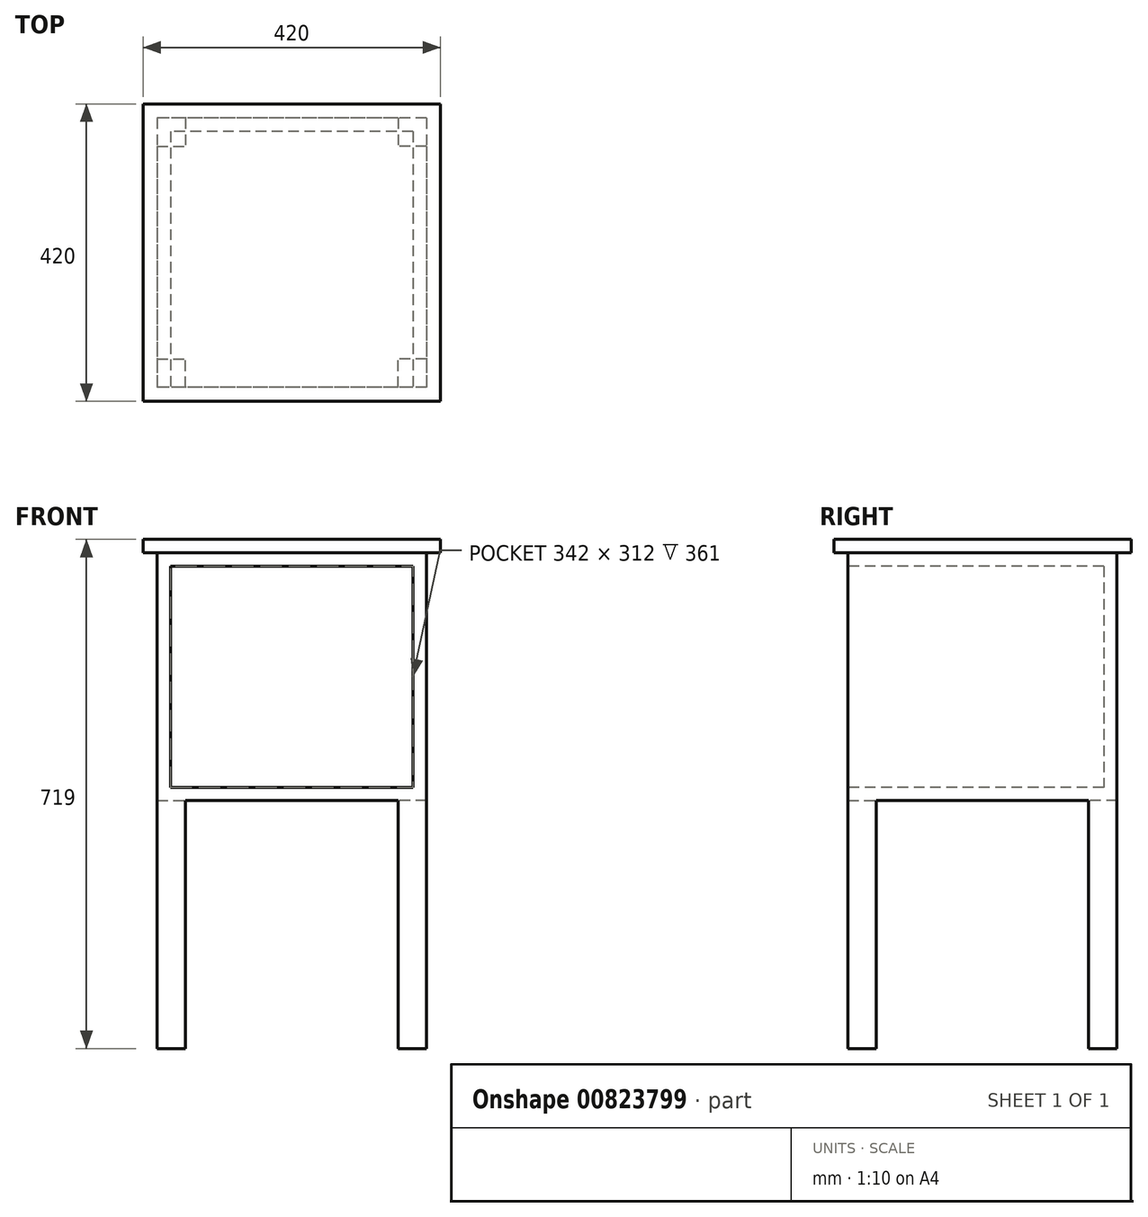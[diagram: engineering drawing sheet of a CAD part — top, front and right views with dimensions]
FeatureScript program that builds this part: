
annotation { "Feature Type Name" : "Feature", "Feature Type Description" : "" }
export const myFeature = defineFeature(function(context is Context, id is Id, definition is map)
    precondition{}
    {
        {
            var Q0;
            Q0=qCreatedBy(makeId("Top.planeOp"),FACE);
            var sketch = newSketch(context, id + "F0", { "sketchPlane" : qUnion([Q0])});
            skLineSegment(sketch, "E0.bottom", {"start": v(190, 190) * mm, "end": v(-190, 190) * mm});
            skLineSegment(sketch, "E0.top", {"start": v(190, -190) * mm, "end": v(-190, -190) * mm});
            skLineSegment(sketch, "E0.left", {"start": v(190, 190) * mm, "end": v(190, -190) * mm});
            skLineSegment(sketch, "E0.right", {"start": v(-190, 190) * mm, "end": v(-190, -190) * mm});
            skPoint(sketch, "E0.middle", {"position": v(0, 0) * mm});
            skSolve(sketch);
        }
        {
            var Q0;
            Q0 = qSketchRegion(id + "F0", true);
            extrude(context, id + "F1", {"entities" : qUnion([Q0]), "depth" : 350 * mm, "offsetDistance" : 25 * mm});
        }
        {
            var Q0;
            Q0=makeQuery(id+"F1.opExtrude","SWEPT_FACE",FACE,{"disambiguationData":[OSD([sQuery(id+"F0.wireOp",EDGE,"E0.top")])]});
            var sketch = newSketch(context, id + "F2", { "sketchPlane" : qUnion([Q0])});
            skLineSegment(sketch, "E1.bottom", {"start": v(171, 19) * mm, "end": v(-171, 19) * mm});
            skLineSegment(sketch, "E1.top", {"start": v(171, 331) * mm, "end": v(-171, 331) * mm});
            skLineSegment(sketch, "E1.left", {"start": v(171, 19) * mm, "end": v(171, 331) * mm});
            skLineSegment(sketch, "E1.right", {"start": v(-171, 19) * mm, "end": v(-171, 331) * mm});
            skPoint(sketch, "E1.middle", {"position": v(0, 175) * mm});
            skPoint(sketch, "E1.middle.positionSnap0", {"position": v(-190, 175) * mm});
            skPoint(sketch, "E1.centerSnap0", {"position": v(-190, 175) * mm});
            skSolve(sketch);
        }
        {
            var Q0;
            Q0=makeQuery(id+"F2.imprint","IMPRINT",FACE,{"disambiguationData":[TD([[makeQuery(id+"F2.imprint","IMPRINT",EDGE,{"derivedFrom":sQuery(id+"F2.wireOp",EDGE,"E1.bottom")}),-1.0]])]});
            extrude(context, id + "F3", {"entities" : qUnion([Q0]), "operationType" : NewBodyOperationType.ADD, "oppositeDirection" : true, "depth" : 361 * mm, "offsetDistance" : 25 * mm});
        }
        {
            var Q0;
            Q0=makeQuery(id+"F1.opExtrude","SWEPT_FACE",FACE,{"disambiguationData":[OSD([sQuery(id+"F0.wireOp",EDGE,"E0.top")])]});
            var sketch = newSketch(context, id + "F4", { "sketchPlane" : qUnion([Q0])});
            skLineSegment(sketch, "E2.bottom", {"start": v(171, 331) * mm, "end": v(-171, 331) * mm});
            skLineSegment(sketch, "E2.top", {"start": v(171, 19) * mm, "end": v(-171, 19) * mm});
            skLineSegment(sketch, "E2.left", {"start": v(171, 331) * mm, "end": v(171, 19) * mm});
            skLineSegment(sketch, "E2.right", {"start": v(-171, 331) * mm, "end": v(-171, 19) * mm});
            skPoint(sketch, "E2.middle", {"position": v(0, 175) * mm});
            skPoint(sketch, "E2.middle.positionSnap0", {"position": v(-190, 175) * mm});
            skPoint(sketch, "E2.centerSnap0", {"position": v(-190, 175) * mm});
            skSolve(sketch);
        }
        {
            var Q0;
            Q0=makeQuery(id+"F4.imprint","IMPRINT",FACE,{"disambiguationData":[TD([[makeQuery(id+"F4.imprint","IMPRINT",EDGE,{"derivedFrom":sQuery(id+"F4.wireOp",EDGE,"E2.bottom")}),1.0]])]});
            extrude(context, id + "F5", {"entities" : qUnion([Q0]), "operationType" : NewBodyOperationType.REMOVE, "oppositeDirection" : true, "depth" : 361 * mm, "offsetDistance" : 25 * mm});
        }
        {
            var Q0;
            Q0=makeQuery(id+"F1.opExtrude","CAP_FACE",FACE,{"disambiguationData":[OSD([sQuery(id+"F0.wireOp",EDGE,"E0.bottom"),sQuery(id+"F0.wireOp",EDGE,"E0.top"),sQuery(id+"F0.wireOp",EDGE,"E0.left"),sQuery(id+"F0.wireOp",EDGE,"E0.right")])],"isStart":true});
            var sketch = newSketch(context, id + "F6", { "sketchPlane" : qUnion([Q0])});
            skLineSegment(sketch, "E3.bottom", {"start": v(-190, 190) * mm, "end": v(-150, 190) * mm});
            skLineSegment(sketch, "E3.top", {"start": v(-190, 150) * mm, "end": v(-150, 150) * mm});
            skLineSegment(sketch, "E3.left", {"start": v(-190, 190) * mm, "end": v(-190, 150) * mm});
            skLineSegment(sketch, "E3.right", {"start": v(-150, 190) * mm, "end": v(-150, 150) * mm});
            skSolve(sketch);
        }
        {
            var Q0;
            Q0=makeQuery(id+"F6.imprint","IMPRINT",FACE,{"disambiguationData":[TD([[makeQuery(id+"F6.imprint","IMPRINT",EDGE,{"derivedFrom":sQuery(id+"F6.wireOp",EDGE,"E3.bottom")}),1.0]])]});
            extrude(context, id + "F7", {"entities" : qUnion([Q0]), "operationType" : NewBodyOperationType.ADD, "depth" : 150 * mm, "offsetDistance" : 25 * mm});
        }
        {
            var Q0;
            Q0=makeQuery(id+"F1.opExtrude","CAP_FACE",FACE,{"disambiguationData":[OSD([sQuery(id+"F0.wireOp",EDGE,"E0.bottom"),sQuery(id+"F0.wireOp",EDGE,"E0.top"),sQuery(id+"F0.wireOp",EDGE,"E0.left"),sQuery(id+"F0.wireOp",EDGE,"E0.right")])],"isStart":true});
            var sketch = newSketch(context, id + "F8", { "sketchPlane" : qUnion([Q0])});
            skLineSegment(sketch, "E4.bottom", {"start": v(190, 190) * mm, "end": v(150, 190) * mm});
            skLineSegment(sketch, "E4.top", {"start": v(190, 150) * mm, "end": v(150, 150) * mm});
            skLineSegment(sketch, "E4.left", {"start": v(190, 190) * mm, "end": v(190, 150) * mm});
            skLineSegment(sketch, "E4.right", {"start": v(150, 190) * mm, "end": v(150, 150) * mm});
            skSolve(sketch);
        }
        {
            var Q0;
            Q0=makeQuery(id+"F8.imprint","IMPRINT",FACE,{"disambiguationData":[TD([[makeQuery(id+"F8.imprint","IMPRINT",EDGE,{"derivedFrom":sQuery(id+"F8.wireOp",EDGE,"E4.bottom")}),1.0]])]});
            extrude(context, id + "F9", {"entities" : qUnion([Q0]), "operationType" : NewBodyOperationType.ADD, "depth" : 150 * mm, "offsetDistance" : 25 * mm});
        }
        {
            var Q0;
            Q0=makeQuery(id+"F1.opExtrude","CAP_FACE",FACE,{"disambiguationData":[OSD([sQuery(id+"F0.wireOp",EDGE,"E0.bottom"),sQuery(id+"F0.wireOp",EDGE,"E0.top"),sQuery(id+"F0.wireOp",EDGE,"E0.left"),sQuery(id+"F0.wireOp",EDGE,"E0.right")])],"isStart":true});
            var sketch = newSketch(context, id + "F10", { "sketchPlane" : qUnion([Q0])});
            skLineSegment(sketch, "E5.bottom", {"start": v(-190, -190) * mm, "end": v(-150, -190) * mm});
            skLineSegment(sketch, "E5.top", {"start": v(-190, -150) * mm, "end": v(-150, -150) * mm});
            skLineSegment(sketch, "E5.left", {"start": v(-190, -190) * mm, "end": v(-190, -150) * mm});
            skLineSegment(sketch, "E5.right", {"start": v(-150, -190) * mm, "end": v(-150, -150) * mm});
            skLineSegment(sketch, "E6.bottom", {"start": v(190, -190) * mm, "end": v(150, -190) * mm});
            skLineSegment(sketch, "E6.top", {"start": v(190, -150) * mm, "end": v(150, -150) * mm});
            skLineSegment(sketch, "E6.left", {"start": v(190, -190) * mm, "end": v(190, -150) * mm});
            skLineSegment(sketch, "E6.right", {"start": v(150, -190) * mm, "end": v(150, -150) * mm});
            skSolve(sketch);
        }
        {
            var Q0;
            Q0=makeQuery(id+"F10.imprint","IMPRINT",FACE,{"disambiguationData":[TD([[makeQuery(id+"F10.imprint","IMPRINT",EDGE,{"derivedFrom":sQuery(id+"F10.wireOp",EDGE,"E5.bottom")}),-1.0]])]});
            extrude(context, id + "F11", {"entities" : qUnion([Q0]), "operationType" : NewBodyOperationType.ADD, "depth" : 150 * mm, "offsetDistance" : 25 * mm});
        }
        {
            var Q0;
            Q0=makeQuery(id+"F1.opExtrude","CAP_FACE",FACE,{"disambiguationData":[OSD([sQuery(id+"F0.wireOp",EDGE,"E0.bottom"),sQuery(id+"F0.wireOp",EDGE,"E0.top"),sQuery(id+"F0.wireOp",EDGE,"E0.left"),sQuery(id+"F0.wireOp",EDGE,"E0.right")])],"isStart":true});
            var sketch = newSketch(context, id + "F12", { "sketchPlane" : qUnion([Q0])});
            skLineSegment(sketch, "E7.bottom", {"start": v(190, -190) * mm, "end": v(150, -190) * mm});
            skLineSegment(sketch, "E7.top", {"start": v(190, -150) * mm, "end": v(150, -150) * mm});
            skLineSegment(sketch, "E7.left", {"start": v(190, -190) * mm, "end": v(190, -150) * mm});
            skLineSegment(sketch, "E7.right", {"start": v(150, -190) * mm, "end": v(150, -150) * mm});
            skSolve(sketch);
        }
        {
            var Q0;
            Q0=makeQuery(id+"F12.imprint","IMPRINT",FACE,{"disambiguationData":[TD([[makeQuery(id+"F12.imprint","IMPRINT",EDGE,{"derivedFrom":sQuery(id+"F12.wireOp",EDGE,"E7.bottom")}),-1.0]])]});
            extrude(context, id + "F13", {"entities" : qUnion([Q0]), "operationType" : NewBodyOperationType.ADD, "depth" : 150 * mm, "offsetDistance" : 25 * mm});
        }
        {
            var Q0;
            Q0=makeQuery(id+"F1.opExtrude","CAP_FACE",FACE,{"disambiguationData":[OSD([sQuery(id+"F0.wireOp",EDGE,"E0.bottom"),sQuery(id+"F0.wireOp",EDGE,"E0.top"),sQuery(id+"F0.wireOp",EDGE,"E0.left"),sQuery(id+"F0.wireOp",EDGE,"E0.right")])],"isStart":false});
            var sketch = newSketch(context, id + "F14", { "sketchPlane" : qUnion([Q0])});
            skLineSegment(sketch, "E8.bottom", {"start": v(210, -210) * mm, "end": v(-210, -210) * mm});
            skLineSegment(sketch, "E8.top", {"start": v(210, 210) * mm, "end": v(-210, 210) * mm});
            skLineSegment(sketch, "E8.left", {"start": v(210, -210) * mm, "end": v(210, 210) * mm});
            skLineSegment(sketch, "E8.right", {"start": v(-210, -210) * mm, "end": v(-210, 210) * mm});
            skPoint(sketch, "E8.middle", {"position": v(0, 0) * mm});
            skSolve(sketch);
        }
        {
            var Q0;
            Q0=makeQuery(id+"F14.imprint","IMPRINT",FACE,{"disambiguationData":[TD([[makeQuery(id+"F14.imprint","IMPRINT",EDGE,{"derivedFrom":makeQuery(id+"F1.opExtrude","CAP_EDGE",EDGE,{"disambiguationData":[OSD([sQuery(id+"F0.wireOp",EDGE,"E0.bottom")])],"isStart":false})}),1.0]])]});
            var Q1;
            Q1=makeQuery(id+"F14.imprint","IMPRINT",FACE,{"disambiguationData":[TD([[makeQuery(id+"F14.imprint","IMPRINT",EDGE,{"derivedFrom":sQuery(id+"F14.wireOp",EDGE,"E8.bottom")}),-1.0]])]});
            extrude(context, id + "F15", {"entities" : qUnion([Q0, Q1]), "operationType" : NewBodyOperationType.ADD, "depth" : 19 * mm, "offsetDistance" : 25 * mm});
        }
        {
            var Q0;
            Q0=makeQuery(id+"F7.opExtrude","CAP_FACE",FACE,{"disambiguationData":[OSD([sQuery(id+"F6.wireOp",EDGE,"E3.bottom"),sQuery(id+"F6.wireOp",EDGE,"E3.top"),sQuery(id+"F6.wireOp",EDGE,"E3.left"),sQuery(id+"F6.wireOp",EDGE,"E3.right")])],"isStart":false});
            var Q1;
            Q1=makeQuery(id+"F9.opExtrude","CAP_FACE",FACE,{"disambiguationData":[OSD([sQuery(id+"F8.wireOp",EDGE,"E4.bottom"),sQuery(id+"F8.wireOp",EDGE,"E4.top"),sQuery(id+"F8.wireOp",EDGE,"E4.left"),sQuery(id+"F8.wireOp",EDGE,"E4.right")])],"isStart":false});
            var Q2;
            Q2=makeQuery(id+"F11.opExtrude","CAP_FACE",FACE,{"disambiguationData":[OSD([sQuery(id+"F10.wireOp",EDGE,"E5.bottom"),sQuery(id+"F10.wireOp",EDGE,"E5.top"),sQuery(id+"F10.wireOp",EDGE,"E5.left"),sQuery(id+"F10.wireOp",EDGE,"E5.right")])],"isStart":false});
            var Q3;
            Q3=makeQuery(id+"F13.opExtrude","CAP_FACE",FACE,{"disambiguationData":[OSD([sQuery(id+"F12.wireOp",EDGE,"E7.bottom"),sQuery(id+"F12.wireOp",EDGE,"E7.top"),sQuery(id+"F12.wireOp",EDGE,"E7.left"),sQuery(id+"F12.wireOp",EDGE,"E7.right")])],"isStart":false});
            extrude(context, id + "F16", {"entities" : qUnion([Q0, Q1, Q2, Q3]), "operationType" : NewBodyOperationType.ADD, "depth" : 200 * mm, "offsetDistance" : 25 * mm});
        }
    });
